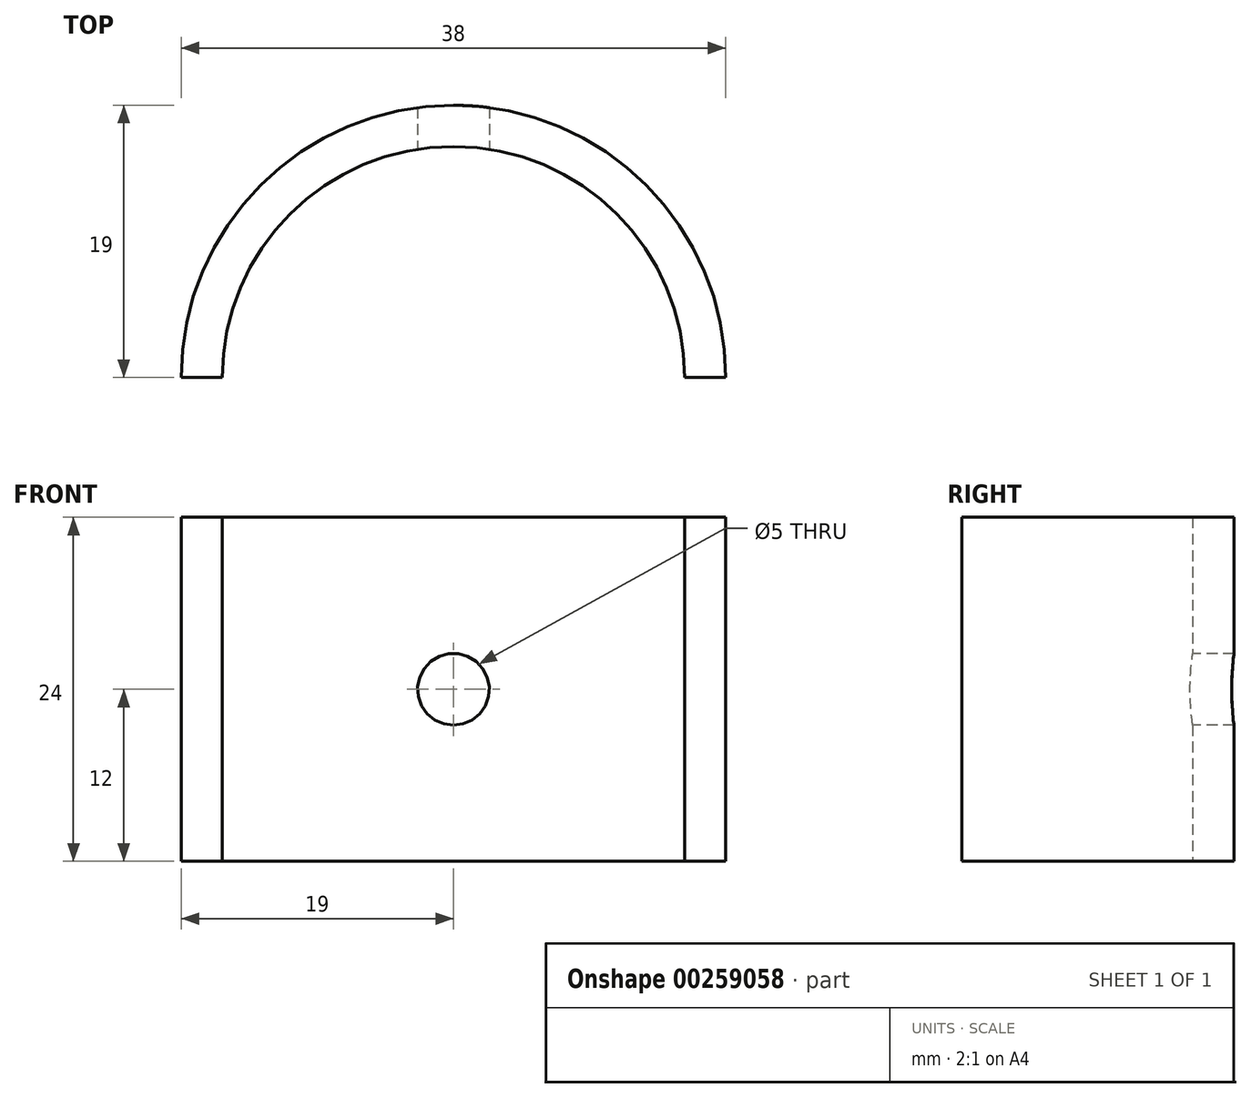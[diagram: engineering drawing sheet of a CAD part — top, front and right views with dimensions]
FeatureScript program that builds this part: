
annotation { "Feature Type Name" : "Feature", "Feature Type Description" : "" }
export const myFeature = defineFeature(function(context is Context, id is Id, definition is map)
    precondition{}
    {
        {
            var Q0;
            Q0=qCreatedBy(makeId("Top.planeOp"),FACE);
            var sketch = newSketch(context, id + "F0", { "sketchPlane" : qUnion([Q0])});
            skCircle(sketch, "E0", {"center": v(0, 0) * mm, "radius": 19 * mm, "construction": true});
            skCircle(sketch, "E1", {"center": v(0, 0) * mm, "radius": 16.12 * mm, "construction": true});
            skArc(sketch, "E2", {"start": v(19, 0) * mm, "mid": v(0, 19) * mm, "end": v(-19, 0) * mm});
            skArc(sketch, "E3", {"start": v(16.12, 0) * mm, "mid": v(0, 16.12) * mm, "end": v(-16.12, 0) * mm});
            skLineSegment(sketch, "E4", {"start": v(-19, 0) * mm, "end": v(-16.12, 0) * mm});
            skLineSegment(sketch, "E5", {"start": v(16.12, 0) * mm, "end": v(19, 0) * mm});
            skSolve(sketch);
        }
        {
            var Q0;
            Q0 = qSketchRegion(id + "F0", true);
            extrude(context, id + "F1", {"entities" : qUnion([Q0]), "depth" : 24 * mm, "offsetDistance" : 25 * mm});
        }
        {
            var Q0;
            Q0=qCreatedBy(makeId("Front.planeOp"),FACE);
            var sketch = newSketch(context, id + "F2", { "sketchPlane" : qUnion([Q0])});
            skCircle(sketch, "E6", {"center": v(0, 12) * mm, "radius": 2.5 * mm});
            skSolve(sketch);
        }
        {
            var Q0;
            Q0 = qSketchRegion(id + "F2", true);
            extrude(context, id + "F3", {"entities" : qUnion([Q0]), "operationType" : NewBodyOperationType.REMOVE, "oppositeDirection" : true, "depth" : 25 * mm, "offsetDistance" : 25 * mm});
        }
    });
